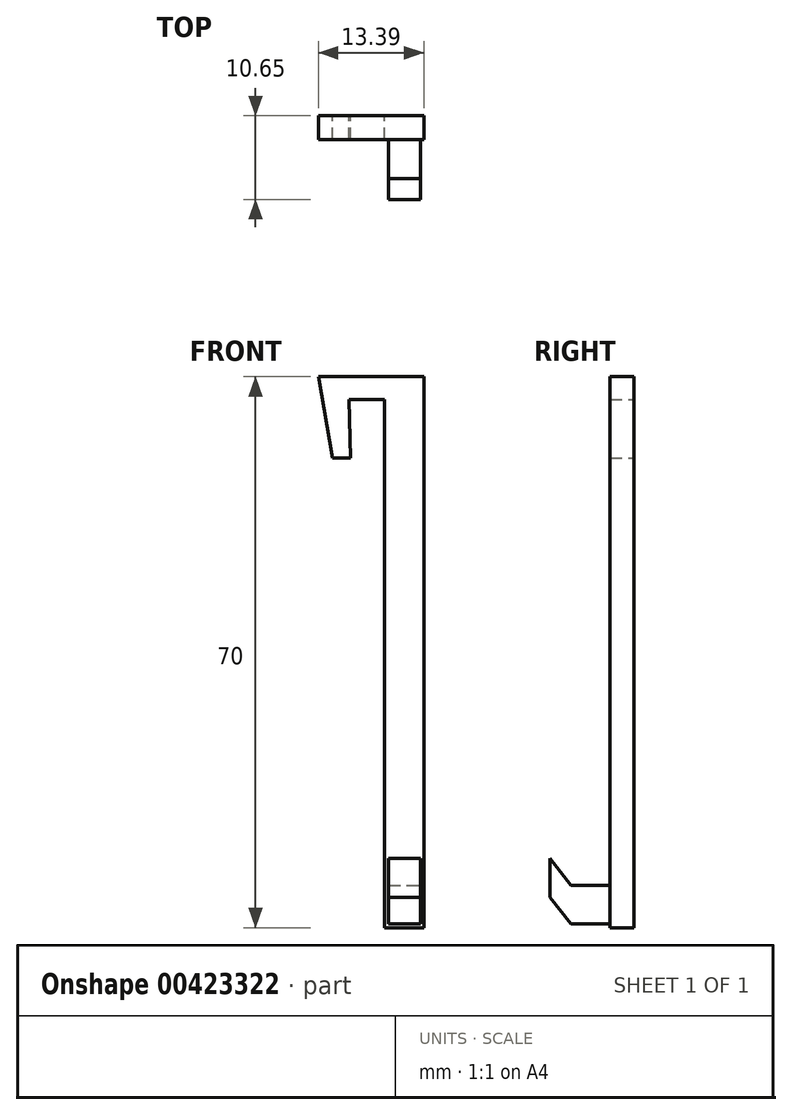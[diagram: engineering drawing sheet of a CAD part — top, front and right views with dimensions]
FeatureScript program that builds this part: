
annotation { "Feature Type Name" : "Feature", "Feature Type Description" : "" }
export const myFeature = defineFeature(function(context is Context, id is Id, definition is map)
    precondition{}
    {
        {
            var Q0;
            Q0=qCreatedBy(makeId("Front.planeOp"),FACE);
            var sketch = newSketch(context, id + "F0", { "sketchPlane" : qUnion([Q0])});
            skLineSegment(sketch, "E0.bottom", {"start": v(1.37, 0) * mm, "end": v(6.37, 0) * mm});
            skLineSegment(sketch, "E0.top", {"start": v(1.37, 70) * mm, "end": v(6.37, 70) * mm});
            skLineSegment(sketch, "E0.left", {"start": v(1.37, 0) * mm, "end": v(1.37, 67.13) * mm});
            skLineSegment(sketch, "E0.right", {"start": v(6.37, 0) * mm, "end": v(6.37, 70) * mm});
            skLineSegment(sketch, "E1", {"start": v(1.37, 70) * mm, "end": v(-7.02, 70) * mm});
            skLineSegment(sketch, "E2", {"start": v(-7.02, 70) * mm, "end": v(-5.24, 59.64) * mm});
            skLineSegment(sketch, "E3", {"start": v(-5.24, 59.64) * mm, "end": v(-2.93, 59.64) * mm});
            skLineSegment(sketch, "E4", {"start": v(-2.93, 59.64) * mm, "end": v(-3.16, 67.13) * mm});
            skLineSegment(sketch, "E5", {"start": v(-3.16, 67.13) * mm, "end": v(1.37, 67.13) * mm});
            skSolve(sketch);
        }
        {
            var Q0;
            Q0 = qSketchRegion(id + "F0", true);
            extrude(context, id + "F1", {"entities" : qUnion([Q0]), "depth" : 3 * mm});
        }
        {
            var Q0;
            Q0=makeQuery(id+"F1.opExtrude","CAP_FACE",FACE,{"disambiguationData":[OSD([sQuery(id+"F0.wireOp",EDGE,"E0.bottom"),sQuery(id+"F0.wireOp",EDGE,"E0.top"),sQuery(id+"F0.wireOp",EDGE,"E0.left"),sQuery(id+"F0.wireOp",EDGE,"E0.right"),sQuery(id+"F0.wireOp",EDGE,"E1"),sQuery(id+"F0.wireOp",EDGE,"E2"),sQuery(id+"F0.wireOp",EDGE,"E3"),sQuery(id+"F0.wireOp",EDGE,"E4"),sQuery(id+"F0.wireOp",EDGE,"E5")])],"isStart":false});
            var sketch = newSketch(context, id + "F2", { "sketchPlane" : qUnion([Q0])});
            skLineSegment(sketch, "E6.bottom", {"start": v(1.87, 5.4) * mm, "end": v(5.9, 5.4) * mm});
            skLineSegment(sketch, "E6.top", {"start": v(1.87, 0.5) * mm, "end": v(5.9, 0.5) * mm});
            skLineSegment(sketch, "E6.left", {"start": v(1.87, 5.4) * mm, "end": v(1.87, 0.5) * mm});
            skLineSegment(sketch, "E6.right", {"start": v(5.9, 5.4) * mm, "end": v(5.9, 0.5) * mm});
            skSolve(sketch);
        }
        {
            var Q0;
            Q0 = qSketchRegion(id + "F2", true);
            extrude(context, id + "F3", {"entities" : qUnion([Q0]), "operationType" : NewBodyOperationType.ADD, "depth" : 5 * mm});
        }
        {
            var Q0;
            Q0=makeQuery(id+"F3.opExtrude","CAP_FACE",FACE,{"disambiguationData":[OSD([sQuery(id+"F2.wireOp",EDGE,"E6.bottom"),sQuery(id+"F2.wireOp",EDGE,"E6.top"),sQuery(id+"F2.wireOp",EDGE,"E6.left"),sQuery(id+"F2.wireOp",EDGE,"E6.right")])],"isStart":false});
            var sketch = newSketch(context, id + "F4", { "sketchPlane" : qUnion([Q0])});
            skSolve(sketch);
        }
        {
            var Q0;
            Q0=makeQuery(id+"F3.opExtrude","SWEPT_FACE",FACE,{"disambiguationData":[OSD([sQuery(id+"F2.wireOp",EDGE,"E6.right")])]});
            var sketch = newSketch(context, id + "F5", { "sketchPlane" : qUnion([Q0])});
            skLineSegment(sketch, "E7", {"start": v(-8, 5.4) * mm, "end": v(-10.65, 8.8) * mm});
            skSolve(sketch);
        }
        {
            var Q0;
            Q0=makeQuery(id+"F4.imprint","IMPRINT",FACE,{"disambiguationData":[TD([[makeQuery(id+"F4.imprint","IMPRINT",EDGE,{"derivedFrom":makeQuery(id+"F3.opExtrude","CAP_EDGE",EDGE,{"disambiguationData":[OSD([sQuery(id+"F2.wireOp",EDGE,"E6.bottom")])],"isStart":false})}),-1.0]])]});
            var Q1;
            Q1=sQuery(id+"F5.wireOp",EDGE,"E7");
            sweep(context, id + "F6", {"operationType" : NewBodyOperationType.ADD, "profiles" : qUnion([Q0]), "path" : qUnion([Q1])});
        }
    });
